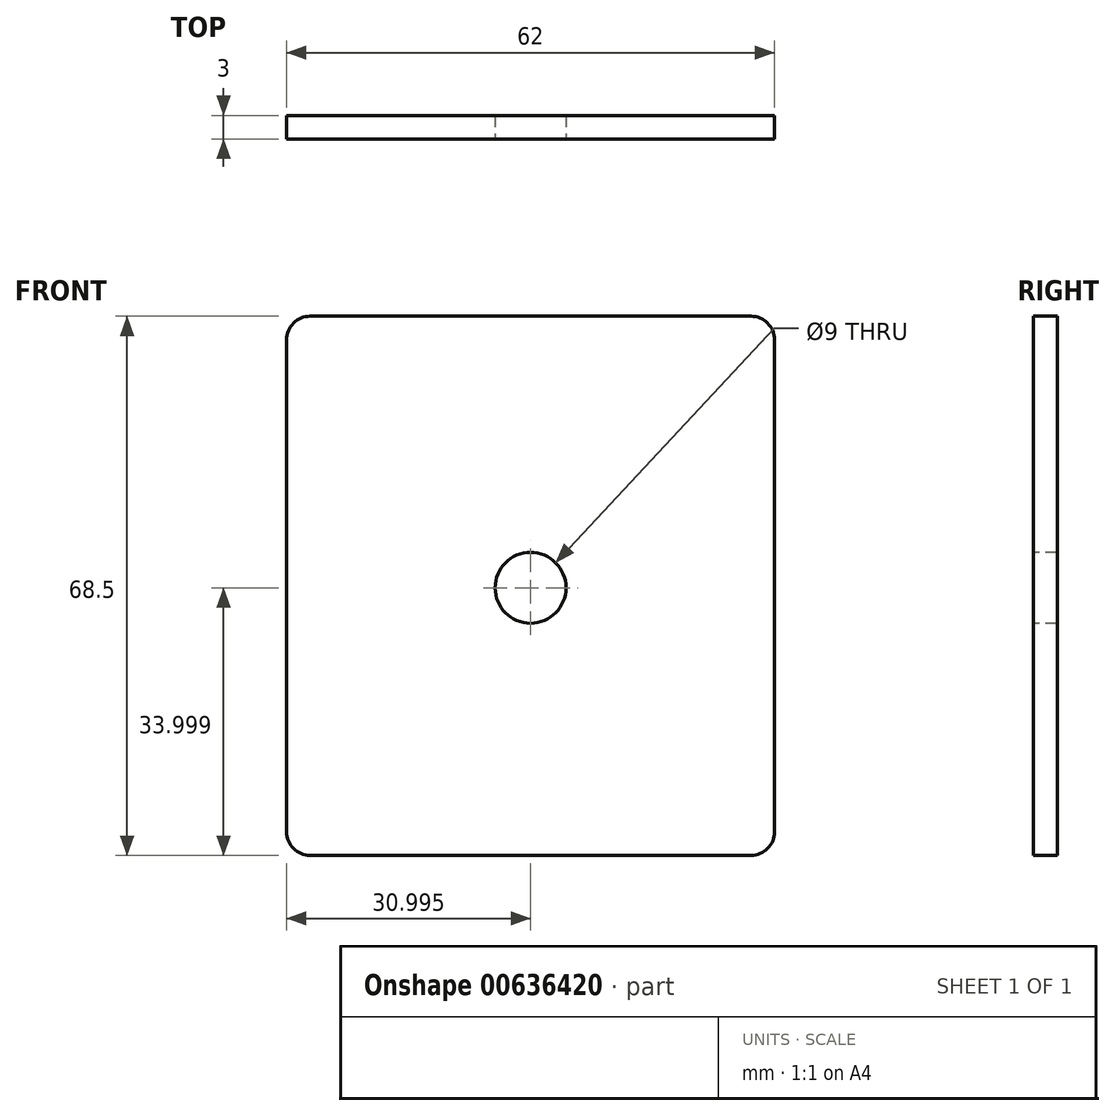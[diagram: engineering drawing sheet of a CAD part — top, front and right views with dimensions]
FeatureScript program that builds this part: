
annotation { "Feature Type Name" : "Feature", "Feature Type Description" : "" }
export const myFeature = defineFeature(function(context is Context, id is Id, definition is map)
    precondition{}
    {
        {
            var Q0;
            Q0=qCreatedBy(makeId("Front.planeOp"),FACE);
            var sketch = newSketch(context, id + "F0", { "sketchPlane" : qUnion([Q0])});
            skLineSegment(sketch, "E0.bottom", {"start": v(-41.86, 37.54) * mm, "end": v(14.14, 37.54) * mm});
            skLineSegment(sketch, "E0.top", {"start": v(-41.86, -30.96) * mm, "end": v(14.14, -30.96) * mm});
            skLineSegment(sketch, "E0.left", {"start": v(-44.86, 34.54) * mm, "end": v(-44.86, -27.96) * mm});
            skLineSegment(sketch, "E0.right", {"start": v(17.14, 34.54) * mm, "end": v(17.14, -27.96) * mm});
            skPoint(sketch, "E1.visualSharp", {"position": v(-44.86, 37.54) * mm});
            skArc(sketch, "E1.filletArc", {"start": v(-41.86, 37.54) * mm, "mid": v(-43.99, 36.66) * mm, "end": v(-44.86, 34.54) * mm});
            skPoint(sketch, "E2.visualSharp", {"position": v(17.14, 37.54) * mm});
            skArc(sketch, "E2.filletArc", {"start": v(17.14, 34.54) * mm, "mid": v(16.26, 36.66) * mm, "end": v(14.14, 37.54) * mm});
            skPoint(sketch, "E3.visualSharp", {"position": v(17.14, -30.96) * mm});
            skArc(sketch, "E3.filletArc", {"start": v(14.14, -30.96) * mm, "mid": v(16.26, -30.08) * mm, "end": v(17.14, -27.96) * mm});
            skPoint(sketch, "E4.visualSharp", {"position": v(-44.86, -30.96) * mm});
            skArc(sketch, "E4.filletArc", {"start": v(-44.86, -27.96) * mm, "mid": v(-43.99, -30.08) * mm, "end": v(-41.86, -30.96) * mm});
            skSolve(sketch);
        }
        {
            var Q0;
            Q0=qSketchRegion(id+"F0",true);
            extrude(context, id + "F1", {"entities" : qUnion([Q0]), "depth" : 3 * mm, "offsetDistance" : 25 * mm});
        }
        {
            var Q0;
            Q0=makeQuery(id+"F1.opExtrude","CAP_FACE",FACE,{"disambiguationData":[OSD([sQuery(id+"F0.wireOp",EDGE,"E0.bottom"),sQuery(id+"F0.wireOp",EDGE,"E0.top"),sQuery(id+"F0.wireOp",EDGE,"E0.left"),sQuery(id+"F0.wireOp",EDGE,"E0.right"),sQuery(id+"F0.wireOp",EDGE,"E1.filletArc"),sQuery(id+"F0.wireOp",EDGE,"E2.filletArc"),sQuery(id+"F0.wireOp",EDGE,"E3.filletArc"),sQuery(id+"F0.wireOp",EDGE,"E4.filletArc")])],"isStart":false});
            var sketch = newSketch(context, id + "F2", { "sketchPlane" : qUnion([Q0])});
            skCircle(sketch, "E5", {"center": v(-13.86, 3.04) * mm, "radius": 4.5 * mm});
            skSolve(sketch);
        }
        {
            var Q0;
            Q0=makeQuery(id+"F2.imprint","IMPRINT",FACE,{"disambiguationData":[TD([[makeQuery(id+"F2.imprint","IMPRINT",EDGE,{"derivedFrom":sQuery(id+"F2.wireOp",EDGE,"E5")}),1.0]])]});
            extrude(context, id + "F3", {"entities" : qUnion([Q0]), "operationType" : NewBodyOperationType.REMOVE, "oppositeDirection" : true, "depth" : 25 * mm, "offsetDistance" : 25 * mm});
        }
    });
